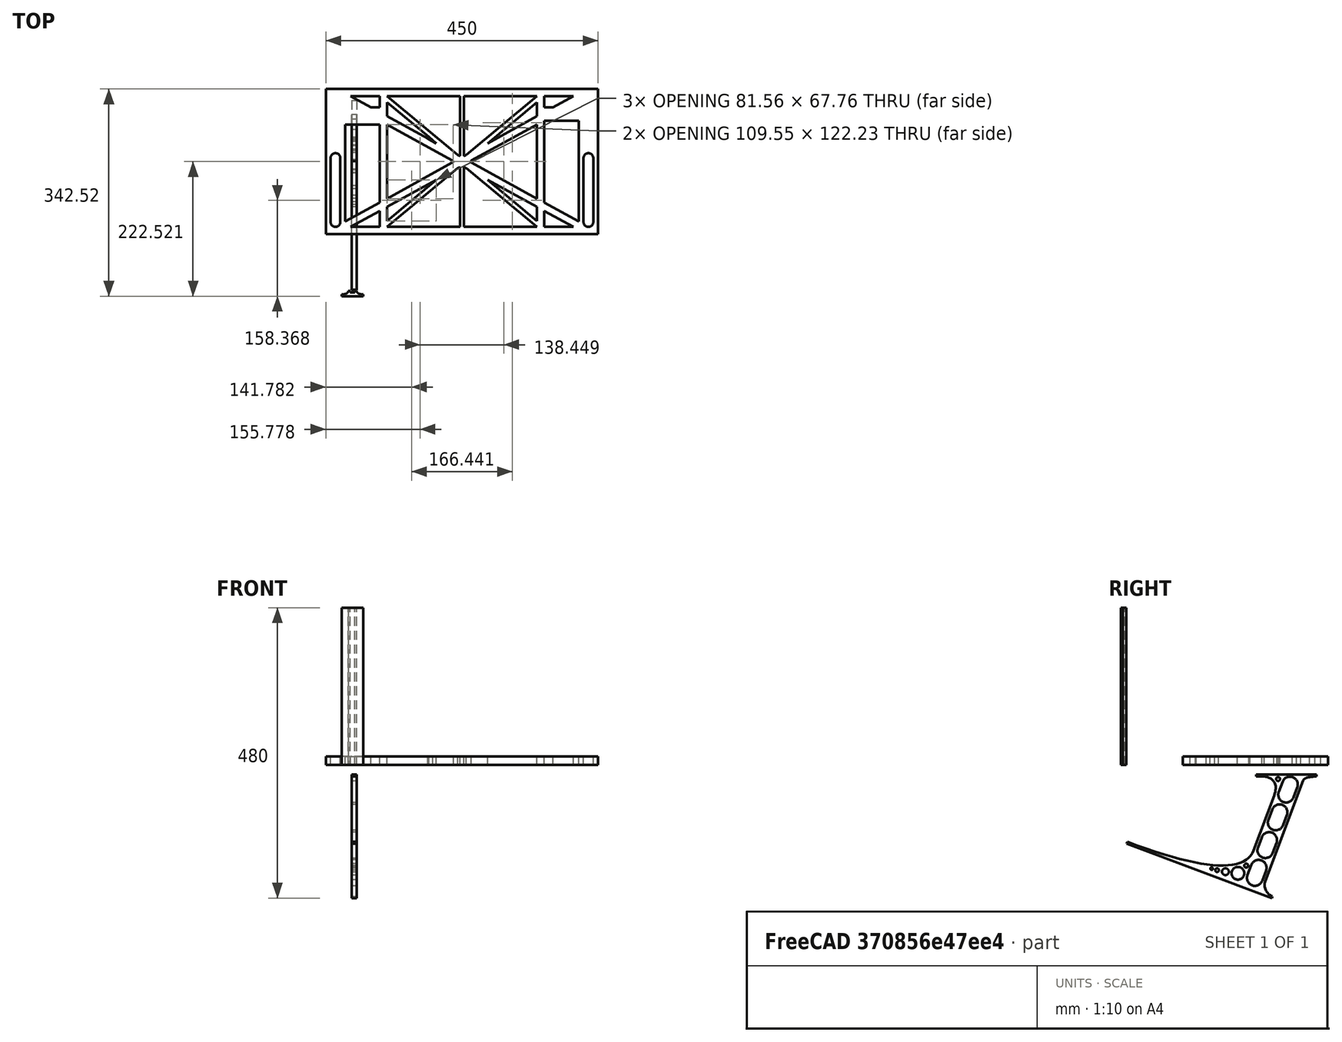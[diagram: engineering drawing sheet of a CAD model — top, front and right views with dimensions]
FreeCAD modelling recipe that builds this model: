
FCSTD DOCUMENT  (FreeCAD 0.19R0.19.2)
Label: laptopStand065
License: All rights reserved
LicenseURL: http://en.wikipedia.org/wiki/All_rights_reserved
objects: Sketcher::SketchObject×3, Part::Extrusion×3
note: 6 computed .brp shape members not serialized (recipe doc carries the construction recipe); baked Part::Feature solids carry a one-line shape summary decoded from their .brp

FEATURE [Sketcher::SketchObject] Sketch
  FullyConstrained = true
  sketch-geometry (104):
    g0: LineSegment StartX=-10.9272 StartY=-82.7794 StartZ=0 EndX=46.0728 EndY=-51.4823 EndZ=0
    g1: LineSegment StartX=366.073 StartY=-91.7794 StartZ=0 EndX=318.073 EndY=-65.424 EndZ=0
    g2: LineSegment StartX=-10.9272 StartY=77.3346 StartZ=0 EndX=-10.9272 EndY=-82.7794 EndZ=0
    g3: LineSegment StartX=375.073 StartY=-82.7794 StartZ=0 EndX=375.073 EndY=83.9235 EndZ=0
    g4: LineSegment StartX=-1.92719 StartY=-91.7794 StartZ=0 EndX=46.0728 EndY=-91.7794 EndZ=0
    g5: LineSegment StartX=318.073 StartY=124.221 StartZ=0 EndX=366.073 EndY=124.221 EndZ=0
    g6: LineSegment StartX=306.073 StartY=-81.8102 StartZ=0 EndX=224.513 EndY=-14.0532 EndZ=0
    g7: LineSegment StartX=306.073 StartY=124.221 StartZ=0 EndX=189.124 EndY=27.0628 EndZ=0
    g8: LineSegment StartX=58.0728 StartY=-91.7794 StartZ=0 EndX=175.022 EndY=5.37834 EndZ=0
    g9: LineSegment StartX=58.0728 StartY=-81.8102 StartZ=0 EndX=58.0728 EndY=-58.8351 EndZ=0
    g10: LineSegment StartX=306.073 StartY=114.251 StartZ=0 EndX=306.073 EndY=91.2763 EndZ=0
    g11: LineSegment StartX=224.513 StartY=46.4944 StartZ=0 EndX=306.073 EndY=114.251 EndZ=0
    g12: LineSegment StartX=175.022 StartY=27.0628 StartZ=0 EndX=58.0728 EndY=124.221 EndZ=0
    g13: LineSegment StartX=139.632 StartY=-14.0532 StartZ=0 EndX=58.0728 EndY=-81.8102 EndZ=0
    g14: LineSegment StartX=224.513 StartY=46.4944 StartZ=0 EndX=306.073 EndY=91.2763 EndZ=0
    g15: LineSegment StartX=139.632 StartY=-14.0532 StartZ=0 EndX=58.0728 EndY=-58.8351 EndZ=0
    g16: LineSegment StartX=189.124 StartY=5.37834 StartZ=0 EndX=306.073 EndY=-91.7794 EndZ=0
    g17: LineSegment StartX=306.073 StartY=77.3346 StartZ=0 EndX=306.073 EndY=-44.8935 EndZ=0
    g18: LineSegment StartX=318.073 StartY=83.9235 StartZ=0 EndX=318.073 EndY=-51.4823 EndZ=0
    g19: LineSegment StartX=306.073 StartY=-58.8351 StartZ=0 EndX=224.513 EndY=-14.0532 EndZ=0
    g20: LineSegment StartX=306.073 StartY=-58.8351 StartZ=0 EndX=306.073 EndY=-81.8102 EndZ=0
    g21: LineSegment StartX=318.073 StartY=-51.4823 StartZ=0 EndX=375.073 EndY=-82.7794 EndZ=0
    g22: LineSegment StartX=318.073 StartY=-65.424 StartZ=0 EndX=318.073 EndY=-91.7794 EndZ=0
    g23: LineSegment StartX=318.073 StartY=-91.7794 StartZ=0 EndX=366.073 EndY=-91.7794 EndZ=0
    g24: LineSegment StartX=58.0728 StartY=-44.8935 StartZ=0 EndX=58.0728 EndY=77.3346 EndZ=0
    g25: LineSegment StartX=46.0728 StartY=-65.424 StartZ=0 EndX=-1.92719 EndY=-91.7794 EndZ=0
    g26: LineSegment StartX=46.0728 StartY=-65.424 StartZ=0 EndX=46.0728 EndY=-91.7794 EndZ=0
    g27: LineSegment StartX=58.0728 StartY=91.2763 StartZ=0 EndX=58.0728 EndY=114.251 EndZ=0
    g28: LineSegment StartX=46.0728 StartY=77.3346 StartZ=0 EndX=46.0728 EndY=-51.4823 EndZ=0
    g29: LineSegment StartX=-42.9272 StartY=136.221 StartZ=0 EndX=-42.9272 EndY=-103.779 EndZ=0
    g30: LineSegment StartX=407.073 StartY=136.221 StartZ=0 EndX=407.073 EndY=-103.779 EndZ=0
    g31: LineSegment StartX=179.022 StartY=27.0628 StartZ=0 EndX=179.022 EndY=124.221 EndZ=0
    g32: LineSegment StartX=185.124 StartY=27.0628 StartZ=0 EndX=185.124 EndY=124.221 EndZ=0
    g33: ArcOfCircle CenterX=-26.9272 CenterY=22.1087 CenterZ=0 NormalX=0 NormalY=0 NormalZ=1 AngleXU=0 Radius=8 StartAngle=1e-16 EndAngle=3.14159
    g34: ArcOfCircle CenterX=-26.9272 CenterY=-83.7794 CenterZ=0 NormalX=0 NormalY=0 NormalZ=1 AngleXU=0 Radius=8 StartAngle=3.14159 EndAngle=6.28319
    g35: LineSegment StartX=-34.9272 StartY=22.1087 StartZ=0 EndX=-34.9272 EndY=-83.7794 EndZ=0
    g36: LineSegment StartX=-18.9272 StartY=22.1087 StartZ=0 EndX=-18.9272 EndY=-83.7794 EndZ=0
    g37: LineSegment StartX=185.124 StartY=-91.7794 StartZ=0 EndX=306.073 EndY=-91.7794 EndZ=0
    g38: LineSegment StartX=179.022 StartY=-91.7794 StartZ=0 EndX=58.0728 EndY=-91.7794 EndZ=0
    g39: LineSegment StartX=306.073 StartY=124.221 StartZ=0 EndX=185.124 EndY=124.221 EndZ=0
    g40: LineSegment StartX=179.022 StartY=124.221 StartZ=0 EndX=58.0728 EndY=124.221 EndZ=0
    g41: ArcOfCircle CenterX=391.073 CenterY=22.1087 CenterZ=0 NormalX=0 NormalY=0 NormalZ=1 AngleXU=0 Radius=8 StartAngle=-4.4e-15 EndAngle=3.14159
    g42: LineSegment StartX=399.073 StartY=22.1087 StartZ=0 EndX=399.073 EndY=-83.7794 EndZ=0
    g43: LineSegment StartX=383.073 StartY=22.1087 StartZ=0 EndX=383.073 EndY=-83.7794 EndZ=0
    g44: ArcOfCircle CenterX=391.073 CenterY=-83.7794 CenterZ=0 NormalX=0 NormalY=0 NormalZ=1 AngleXU=0 Radius=8 StartAngle=3.14159 EndAngle=6.28319
    g45: Circle CenterX=175.022 CenterY=27.0628 CenterZ=0 NormalX=0 NormalY=0 NormalZ=1 AngleXU=0 Radius=1
    g46: Circle CenterX=179.022 CenterY=24.8665 CenterZ=0 NormalX=0 NormalY=0 NormalZ=1 AngleXU=0 Radius=1
    g47: Circle CenterX=179.022 CenterY=27.0628 CenterZ=0 NormalX=0 NormalY=0 NormalZ=1 AngleXU=0 Radius=1
    g48: BSplineCurve PolesCount=3 KnotsCount=2 Degree=2 IsPeriodic=0
    g49: GeomPoint X=175.022 Y=27.0628 Z=0
    g50: GeomPoint X=179.022 Y=27.0628 Z=0
    g51: Circle CenterX=189.124 CenterY=27.0628 CenterZ=0 NormalX=0 NormalY=0 NormalZ=1 AngleXU=0 Radius=1
    g52: Circle CenterX=185.124 CenterY=24.8665 CenterZ=0 NormalX=0 NormalY=0 NormalZ=1 AngleXU=0 Radius=1
    g53: Circle CenterX=185.124 CenterY=27.0628 CenterZ=0 NormalX=0 NormalY=0 NormalZ=1 AngleXU=0 Radius=1
    g54: BSplineCurve PolesCount=3 KnotsCount=2 Degree=2 IsPeriodic=0
    g55: GeomPoint X=189.124 Y=27.0628 Z=0
    g56: GeomPoint X=185.124 Y=27.0628 Z=0
    g57: Circle CenterX=175.022 CenterY=5.37834 CenterZ=0 NormalX=0 NormalY=0 NormalZ=1 AngleXU=0 Radius=1
    g58: Circle CenterX=179.022 CenterY=7.57463 CenterZ=0 NormalX=0 NormalY=0 NormalZ=1 AngleXU=0 Radius=1
    g59: Circle CenterX=179.022 CenterY=5.34704 CenterZ=0 NormalX=0 NormalY=0 NormalZ=1 AngleXU=0 Radius=1
    g60: BSplineCurve PolesCount=3 KnotsCount=2 Degree=2 IsPeriodic=0
    g61: GeomPoint X=175.022 Y=5.37834 Z=0
    g62: GeomPoint X=179.022 Y=5.34704 Z=0
    g63: Circle CenterX=189.124 CenterY=5.37834 CenterZ=0 NormalX=0 NormalY=0 NormalZ=1 AngleXU=0 Radius=1
    g64: Circle CenterX=185.124 CenterY=7.57463 CenterZ=0 NormalX=0 NormalY=0 NormalZ=1 AngleXU=0 Radius=1
    g65: Circle CenterX=185.124 CenterY=5.34704 CenterZ=0 NormalX=0 NormalY=0 NormalZ=1 AngleXU=0 Radius=1
    g66: BSplineCurve PolesCount=3 KnotsCount=2 Degree=2 IsPeriodic=0
    g67: GeomPoint X=189.124 Y=5.37834 Z=0
    g68: GeomPoint X=185.124 Y=5.34704 Z=0
    g69: LineSegment StartX=179.022 StartY=5.34704 StartZ=0 EndX=179.022 EndY=-91.7794 EndZ=0
    g70: LineSegment StartX=185.124 StartY=-91.7794 StartZ=0 EndX=185.124 EndY=5.34704 EndZ=0
    g71: Circle CenterX=165.871 CenterY=18.1458 CenterZ=0 NormalX=0 NormalY=0 NormalZ=1 AngleXU=0 Radius=1
    g72: Circle CenterX=169.377 CenterY=16.2206 CenterZ=0 NormalX=0 NormalY=0 NormalZ=1 AngleXU=0 Radius=1
    g73: Circle CenterX=165.871 CenterY=14.2954 CenterZ=0 NormalX=0 NormalY=0 NormalZ=1 AngleXU=0 Radius=1
    g74: BSplineCurve PolesCount=3 KnotsCount=2 Degree=2 IsPeriodic=0
    g75: GeomPoint X=165.871 Y=18.1458 Z=0
    g76: GeomPoint X=165.871 Y=14.2954 Z=0
    g77: Circle CenterX=198.275 CenterY=18.1458 CenterZ=0 NormalX=0 NormalY=0 NormalZ=1 AngleXU=0 Radius=1
    g78: Circle CenterX=194.768 CenterY=16.2206 CenterZ=0 NormalX=0 NormalY=0 NormalZ=1 AngleXU=0 Radius=1
    g79: Circle CenterX=198.275 CenterY=14.2954 CenterZ=0 NormalX=0 NormalY=0 NormalZ=1 AngleXU=0 Radius=1
    g80: BSplineCurve PolesCount=3 KnotsCount=2 Degree=2 IsPeriodic=0
    g81: GeomPoint X=198.275 Y=18.1458 Z=0
    g82: GeomPoint X=198.275 Y=14.2954 Z=0
    g83: LineSegment StartX=165.871 StartY=18.1458 StartZ=0 EndX=58.0728 EndY=77.3346 EndZ=0
    g84: LineSegment StartX=58.0728 StartY=-44.8935 StartZ=0 EndX=165.871 EndY=14.2954 EndZ=0
    g85: LineSegment StartX=198.275 StartY=18.1458 StartZ=0 EndX=306.073 EndY=77.3346 EndZ=0
    g86: LineSegment StartX=198.275 StartY=14.2954 StartZ=0 EndX=306.073 EndY=-44.8935 EndZ=0
    g87: LineSegment StartX=407.073 StartY=-103.779 StartZ=0 EndX=-42.9272 EndY=-103.779 EndZ=0
    g88: LineSegment StartX=407.073 StartY=136.221 StartZ=0 EndX=-42.9272 EndY=136.221 EndZ=0
    g89: LineSegment StartX=46.0728 StartY=77.3346 StartZ=0 EndX=-10.9272 EndY=77.3346 EndZ=0
    g90: LineSegment StartX=46.0728 StartY=105.865 StartZ=0 EndX=31.5028 EndY=105.865 EndZ=0
    g91: LineSegment StartX=46.0728 StartY=124.221 StartZ=0 EndX=46.0728 EndY=105.865 EndZ=0
    g92: LineSegment StartX=-1.92719 StartY=124.221 StartZ=0 EndX=31.5028 EndY=105.865 EndZ=0
    g93: LineSegment StartX=46.0728 StartY=124.221 StartZ=0 EndX=-1.92719 EndY=124.221 EndZ=0
    g94: LineSegment StartX=318.073 StartY=83.9235 StartZ=0 EndX=375.073 EndY=83.9235 EndZ=0
    g95: LineSegment StartX=318.073 StartY=105.865 StartZ=0 EndX=332.643 EndY=105.865 EndZ=0
    g96: LineSegment StartX=332.643 StartY=105.865 StartZ=0 EndX=366.073 EndY=124.221 EndZ=0
    g97: LineSegment StartX=318.073 StartY=124.221 StartZ=0 EndX=318.073 EndY=105.865 EndZ=0
    g98: Circle CenterX=125.607 CenterY=54.1951 CenterZ=0 NormalX=0 NormalY=0 NormalZ=1 AngleXU=0 Radius=1
    g99: Circle CenterX=139.632 CenterY=46.4944 CenterZ=0 NormalX=0 NormalY=0 NormalZ=1 AngleXU=0 Radius=1
    g100: Circle CenterX=127.325 CenterY=56.7187 CenterZ=0 NormalX=0 NormalY=0 NormalZ=1 AngleXU=0 Radius=1
    g101: BSplineCurve PolesCount=3 KnotsCount=2 Degree=2 IsPeriodic=0
    g102: GeomPoint X=125.607 Y=54.1951 Z=0
    g103: GeomPoint X=127.325 Y=56.7187 Z=0
  constraints (194):
    c: Horizontal(g4)
    c: Horizontal(g5)
    c: Coincident(g11,g14)
    c: Coincident(g15,g13)
    c: Coincident(g19,g6)
    c: Coincident(g11,g10)
    c: Tangent(g10,g17)
    c: Coincident(g14,g10)
    c: Coincident(g20,g6)
    c: Tangent(g1,g19)
    c: Tangent(g17,g20)
    c: Coincident(g18,g21)
    c: Coincident(g22,g1)
    c: Tangent(g18,g22)
    c: Coincident(g13,g9)
    c: Tangent(g9,g24)
    c: Coincident(g15,g9)
    c: Tangent(g15,g25)
    c: Coincident(g26,g25)
    c: Coincident(g0,g28)
    c: Tangent(g24,g27)
    c: Block(g12)
    c: Block(g7)
    c: Block(g21)
    c: Block(g3)
    c: Block(g19)
    c: Block(g20)
    c: Block(g1)
    c: Block(g22)
    c: Block(g11)
    c: Block(g16)
    c: Block(g8)
    c: Block(g15)
    c: Block(g13)
    c: Block(g26)
    c: Block(g25)
    c: Block(g0)
    c: Block(g2)
    c: Block(g27)
    c: Block(g17)
    c: Block(g5)
    c: Block(g23)
    c: Block(g4)
    c: Vertical(g29)
    c: Vertical(g30)
    c: Block(g30)
    c: Block(g29)
    c: Vertical(g31)
    c: Vertical(g32)
    c: Block(g31)
    c: Block(g32)
    c: Tangent(g33,g36) = 1.5708
    c: Tangent(g33,g35) = -1.5708
    c: Tangent(g35,g34) = -1.5708
    c: Tangent(g36,g34) = 1.5708
    c: Vertical(g35)
    c: Equal(g33,g34)
    c: Block(g36)
    c: Block(g35)
    c: Coincident(g37,g16)
    c: Horizontal(g37)
    c: Coincident(g38,g8)
    c: Horizontal(g38)
    c: Coincident(g39,g7)
    c: Coincident(g39,g32)
    c: Horizontal(g39)
    c: Coincident(g40,g31)
    c: Coincident(g40,g12)
    c: Horizontal(g40)
    c: Tangent(g41,g42) = 1.5708
    c: Tangent(g42,g44) = 1.5708
    c: Equal(g41,g44)
    c: Coincident(g43,g41)
    c: Coincident(g43,g44)
    c: Block(g42)
    c: Block(g43)
    c: Coincident(g48,g12)
    c: Weight(g45) = 1
    c: Equal(g45,g46)
    c: Equal(g45,g47)
    c: Coincident(g48,g31)
    c: InternalAlignment(g45,g48)
    c: InternalAlignment(g46,g48)
    c: InternalAlignment(g47,g48)
    c: InternalAlignment(g49,g48)
    c: InternalAlignment(g50,g48)
    c: Coincident(g54,g7)
    c: Weight(g51) = 1
    c: Equal(g51,g52)
    c: Equal(g51,g53)
    c: Coincident(g54,g32)
    c: InternalAlignment(g51,g54)
    c: InternalAlignment(g52,g54)
    c: InternalAlignment(g53,g54)
    c: InternalAlignment(g55,g54)
    c: InternalAlignment(g56,g54)
    c: Block(g54)
    c: Block(g48)
    c: Coincident(g60,g8)
    c: Weight(g57) = 1
    c: Equal(g57,g58)
    c: Equal(g57,g59)
    c: InternalAlignment(g57,g60)
    c: InternalAlignment(g58,g60)
    c: InternalAlignment(g59,g60)
    c: InternalAlignment(g61,g60)
    c: InternalAlignment(g62,g60)
    c: Weight(g63) = 1
    c: Equal(g63,g64)
    c: Equal(g63,g65)
    c: InternalAlignment(g63,g66)
    c: InternalAlignment(g64,g66)
    c: InternalAlignment(g65,g66)
    c: InternalAlignment(g67,g66)
    c: InternalAlignment(g68,g66)
    c: Block(g66)
    c: Block(g60)
    c: Coincident(g69,g60)
    c: Coincident(g69,g38)
    c: Vertical(g69)
    c: Coincident(g70,g37)
    c: Coincident(g70,g66)
    c: Vertical(g70)
    c: Weight(g71) = 1
    c: Equal(g71,g72)
    c: Equal(g71,g73)
    c: InternalAlignment(g71,g74)
    c: InternalAlignment(g72,g74)
    c: InternalAlignment(g73,g74)
    c: InternalAlignment(g75,g74)
    c: InternalAlignment(g76,g74)
    c: Weight(g77) = 1
    c: Equal(g77,g78)
    c: Equal(g77,g79)
    c: InternalAlignment(g77,g80)
    c: InternalAlignment(g78,g80)
    c: InternalAlignment(g79,g80)
    c: InternalAlignment(g81,g80)
    c: InternalAlignment(g82,g80)
    c: Block(g74)
    c: Block(g80)
    c: Coincident(g83,g74)
    c: Coincident(g83,g24)
    c: Coincident(g84,g24)
    c: Coincident(g84,g74)
    c: Coincident(g85,g80)
    c: Coincident(g85,g17)
    c: Coincident(g86,g80)
    c: Coincident(g86,g17)
    c: Block(g24)
    c: Coincident(g87,g30)
    c: Coincident(g87,g29)
    c: Horizontal(g87)
    c: Distance(g87) = 450
    c: Coincident(g88,g30)
    c: Coincident(g88,g29)
    c: Horizontal(g88)
    c: Horizontal(g89)
    c: Coincident(g28,g89)
    c: Horizontal(g90)
    c: Vertical(g91)
    c: Block(g91)
    c: Block(g90)
    c: Block(g89)
    c: Distance(g91) = 18.3554
    c: Coincident(g93,g91)
    c: Coincident(g93,g92)
    c: Horizontal(g93)
    c: Block(g93)
    c: Block(g92)
    c: Coincident(g90,g92)
    c: Coincident(g2,g89)
    c: Coincident(g94,g18)
    c: Horizontal(g94)
    c: Horizontal(g95)
    c: Block(g94)
    c: Block(g10)
    c: Coincident(g96,g5)
    c: Coincident(g97,g5)
    c: Coincident(g97,g95)
    c: Vertical(g97)
    c: Block(g97)
    c: Coincident(g95,g96)
    c: Block(g96)
    c: Coincident(g3,g94)
    c: Weight(g98) = 1
    c: Equal(g98,g99)
    c: Equal(g98,g100)
    c: InternalAlignment(g98,g101)
    c: InternalAlignment(g99,g101)
    c: InternalAlignment(g100,g101)
    c: InternalAlignment(g102,g101)
    c: InternalAlignment(g103,g101)
    c: Block(g101)
FEATURE [Sketcher::SketchObject] Sketch001
  FullyConstrained = true
  MapMode = 4
  Placement = pos=(0,0,0) rot=(0.57735,0.57735,0.57735;2.0944rad)
  Support = -> [Sketch]
  sketch-geometry (46):
    g0: BSplineCurve PolesCount=3 KnotsCount=2 Degree=2 IsPeriodic=0
    g1: ArcOfCircle CenterX=73.1223 CenterY=-32.291 CenterZ=0 NormalX=0 NormalY=0 NormalZ=1 AngleXU=0 Radius=13 StartAngle=5.92268 EndAngle=9.06428
    g2: ArcOfCircle CenterX=66.7816 CenterY=-49.1439 CenterZ=0 NormalX=0 NormalY=0 NormalZ=1 AngleXU=0 Radius=13 StartAngle=2.78068 EndAngle=5.92131
    g3: ArcOfCircle CenterX=55.9263 CenterY=-78.1807 CenterZ=0 NormalX=0 NormalY=0 NormalZ=1 AngleXU=0 Radius=13 StartAngle=5.92268 EndAngle=9.06428
    g4: ArcOfCircle CenterX=49.5884 CenterY=-95.0342 CenterZ=0 NormalX=0 NormalY=0 NormalZ=1 AngleXU=0 Radius=13 StartAngle=2.78068 EndAngle=5.92131
    g5: ArcOfCircle CenterX=38.7206 CenterY=-124.067 CenterZ=0 NormalX=0 NormalY=0 NormalZ=1 AngleXU=0 Radius=13 StartAngle=5.92268 EndAngle=9.06428
    g6: ArcOfCircle CenterX=32.3875 CenterY=-140.92 CenterZ=0 NormalX=0 NormalY=0 NormalZ=1 AngleXU=0 Radius=13 StartAngle=2.78068 EndAngle=5.92131
    g7: ArcOfCircle CenterX=21.4715 CenterY=-169.934 CenterZ=0 NormalX=0 NormalY=0 NormalZ=1 AngleXU=0 Radius=13 StartAngle=5.92268 EndAngle=9.06428
    g8: ArcOfCircle CenterX=15.1336 CenterY=-186.787 CenterZ=0 NormalX=0 NormalY=0 NormalZ=1 AngleXU=0 Radius=13 StartAngle=2.78068 EndAngle=5.92131
    g9-g12: Circle x4 (B-spline internal-alignment scaffolding for g13; pole/knot coordinates omitted)
    g13: BSplineCurve PolesCount=4 KnotsCount=2 Degree=3 IsPeriodic=0
    g14: GeomPoint X=28.8094 Y=-19.0875 Z=0
    g15: GeomPoint X=47.0443 Y=-50.4712 Z=0
    g16: Circle CenterX=53.5586 CenterY=-23.2695 CenterZ=0 NormalX=0 NormalY=0 NormalZ=1 AngleXU=0 Radius=3.24518
    g17: Circle CenterX=-195.441 CenterY=-127.082 CenterZ=0 NormalX=0 NormalY=0 NormalZ=1 AngleXU=0 Radius=1
    g18: Circle CenterX=-8.24091 CenterY=-197.481 CenterZ=0 NormalX=0 NormalY=0 NormalZ=1 AngleXU=0 Radius=1
    g19: Circle CenterX=12.8789 CenterY=-141.321 CenterZ=0 NormalX=0 NormalY=0 NormalZ=1 AngleXU=0 Radius=1
    g20: BSplineCurve PolesCount=3 KnotsCount=2 Degree=2 IsPeriodic=0
    g21: GeomPoint X=-195.441 Y=-127.082 Z=0
    g22: GeomPoint X=12.8789 Y=-141.321 Z=0
    g23: Circle CenterX=-12.8016 CenterY=-179.036 CenterZ=0 NormalX=0 NormalY=0 NormalZ=1 AngleXU=0 Radius=10.5072
    g24: Circle CenterX=0.933922 CenterY=-166.43 CenterZ=0 NormalX=0 NormalY=0 NormalZ=1 AngleXU=0 Radius=3.26661
    g25: Circle CenterX=-33.5518 CenterY=-176.44 CenterZ=0 NormalX=0 NormalY=0 NormalZ=1 AngleXU=0 Radius=5.64388
    g26: Circle CenterX=-47.2366 CenterY=-173.859 CenterZ=0 NormalX=0 NormalY=0 NormalZ=1 AngleXU=0 Radius=3.01653
    g27: Circle CenterX=-56.2595 CenterY=-171.456 CenterZ=0 NormalX=0 NormalY=0 NormalZ=1 AngleXU=0 Radius=2.12826
    g28: ArcOfCircle CenterX=51.2151 CenterY=-198.473 CenterZ=0 NormalX=0 NormalY=0 NormalZ=1 AngleXU=0 Radius=20 StartAngle=2.78189 EndAngle=4.35269
    g29: LineSegment StartX=32.4951 StartY=-191.433 StartZ=0 EndX=94.6578 EndY=-26.1352 EndZ=0
    g30: LineSegment StartX=43.1192 StartY=-220.001 StartZ=0 EndX=-196.497 EndY=-129.89 EndZ=0
    g31: LineSegment StartX=43.1192 StartY=-220.001 StartZ=0 EndX=44.1752 EndY=-217.193 EndZ=0
    g32: LineSegment StartX=117.223 StartY=-19.0875 StartZ=0 EndX=117.223 EndY=-16.0875 EndZ=0
    g33: LineSegment StartX=117.223 StartY=-16.0875 StartZ=0 EndX=17.2232 EndY=-16.0875 EndZ=0
    g34: LineSegment StartX=17.2232 StartY=-16.0875 StartZ=0 EndX=17.2232 EndY=-19.0875 EndZ=0
    g35: LineSegment StartX=28.8094 StartY=-19.0875 StartZ=0 EndX=17.2232 EndY=-19.0875 EndZ=0
    g36: LineSegment StartX=47.0443 StartY=-50.4712 StartZ=0 EndX=12.8789 EndY=-141.321 EndZ=0
    g37: LineSegment StartX=-195.441 StartY=-127.082 StartZ=0 EndX=-196.497 EndY=-129.89 EndZ=0
    g38: LineSegment StartX=85.2866 StartY=-36.8766 StartZ=0 EndX=78.9396 EndY=-53.7463 EndZ=0
    g39: LineSegment StartX=60.9579 StartY=-27.7053 StartZ=0 EndX=54.6191 EndY=-44.5532 EndZ=0
    g40: LineSegment StartX=68.0907 StartY=-82.7664 StartZ=0 EndX=61.7465 EndY=-99.6365 EndZ=0
    g41: LineSegment StartX=43.7619 StartY=-73.595 StartZ=0 EndX=37.426 EndY=-90.4435 EndZ=0
    g42: LineSegment StartX=50.885 StartY=-128.652 StartZ=0 EndX=44.5456 EndY=-145.522 EndZ=0
    g43: LineSegment StartX=26.5562 StartY=-119.481 StartZ=0 EndX=20.2251 EndY=-136.329 EndZ=0
    g44: LineSegment StartX=9.3071 StartY=-165.349 StartZ=0 EndX=2.97115 EndY=-182.197 EndZ=0
    g45: LineSegment StartX=33.6358 StartY=-174.52 StartZ=0 EndX=27.2917 EndY=-191.39 EndZ=0
  constraints (71):
    c: Block(g0)
    c: Block(g1)
    c: Block(g2)
    c: Block(g4)
    c: Block(g3)
    c: Block(g6)
    c: Block(g5)
    c: Block(g8)
    c: Block(g7)
    c: Weight(g9) = 1
    c: Equal(g9,g10)
    c: Equal(g9,g11)
    c: Equal(g9,g12)
    c: InternalAlignment(g9-g12 -> g13) x4
    c: InternalAlignment(g14,g13)
    c: InternalAlignment(g15,g13)
    c: Block(g16)
    c: Weight(g17) = 1
    c: Equal(g17,g18)
    c: Equal(g17,g19)
    c: InternalAlignment(g17,g20)
    c: InternalAlignment(g18,g20)
    c: InternalAlignment(g19,g20)
    c: InternalAlignment(g21,g20)
    c: InternalAlignment(g22,g20)
    c: Block(g20)
    c: Block(g23)
    c: Block(g24)
    c: Block(g25)
    c: Block(g26)
    c: Block(g27)
    c: Block(g28)
    c: Coincident(g29,g28)
    c: Coincident(g29,g0)
    c: Block(g13)
    c: Coincident(g31,g30)
    c: Coincident(g31,g28)
    c: Block(g31)
    c: Coincident(g32,g0)
    c: Vertical(g32)
    c: Coincident(g33,g32)
    c: Horizontal(g33)
    c: Coincident(g34,g33)
    c: Vertical(g34)
    c: Block(g33)
    c: Coincident(g35,g13)
    c: Coincident(g35,g34)
    c: Horizontal(g35)
    c: Coincident(g36,g13)
    c: Coincident(g36,g20)
    c: Coincident(g37,g20)
    c: Coincident(g37,g30)
    c: Block(g30)
    c: Coincident(g38,g1)
    c: Coincident(g38,g2)
    c: Coincident(g39,g1)
    c: Coincident(g39,g2)
    c: Coincident(g40,g3)
    c: Coincident(g40,g4)
    c: Coincident(g41,g3)
    c: Coincident(g41,g4)
    c: Coincident(g42,g5)
    c: Coincident(g42,g6)
    c: Coincident(g43,g5)
    c: Coincident(g43,g6)
    c: Coincident(g44,g7)
    c: Coincident(g44,g8)
    c: Coincident(g45,g7)
    c: Coincident(g45,g8)
    c: Distance(g30) = 256
    c: Distance(g33) = 100
FEATURE [Part::Extrusion] Extrude002
  Base = -> Sketch001
  Dir = (1,0,0)
  DirMode = 2
  FaceMakerClass = Part::FaceMakerBullseye
  LengthFwd = 8
  LengthRev = 0
  Solid = true
  Symmetric = false
FEATURE [Sketcher::SketchObject] Sketch002
  FullyConstrained = true
  sketch-geometry (20):
    g0: LineSegment StartX=-2.77179 StartY=-200.304 StartZ=0 EndX=5.22821 EndY=-200.304 EndZ=0
    g1: LineSegment StartX=5.22821 StartY=-200.304 StartZ=0 EndX=5.22821 EndY=-197.304 EndZ=0
    g2: LineSegment StartX=-2.77179 StartY=-200.304 StartZ=0 EndX=-2.77179 EndY=-197.304 EndZ=0
    g3: LineSegment StartX=5.22821 StartY=-197.304 StartZ=0 EndX=8.22821 EndY=-197.304 EndZ=0
    g4: LineSegment StartX=-2.77179 StartY=-197.304 StartZ=0 EndX=-5.77179 EndY=-197.304 EndZ=0
    g5: LineSegment StartX=19.2282 StartY=-203.304 StartZ=0 EndX=19.2282 EndY=-206.304 EndZ=0
    g6: LineSegment StartX=-16.7718 StartY=-203.304 StartZ=0 EndX=-16.7718 EndY=-206.304 EndZ=0
    g7: LineSegment StartX=-16.7718 StartY=-206.304 StartZ=0 EndX=19.2282 EndY=-206.304 EndZ=0
    g8: Circle CenterX=-16.7718 CenterY=-203.304 CenterZ=0 NormalX=0 NormalY=0 NormalZ=1 AngleXU=0 Radius=1
    g9: Circle CenterX=-5.77179 CenterY=-203.304 CenterZ=0 NormalX=0 NormalY=0 NormalZ=1 AngleXU=0 Radius=1
    g10: Circle CenterX=-5.77179 CenterY=-197.304 CenterZ=0 NormalX=0 NormalY=0 NormalZ=1 AngleXU=0 Radius=1
    g11: BSplineCurve PolesCount=3 KnotsCount=2 Degree=2 IsPeriodic=0
    g12: GeomPoint X=-16.7718 Y=-203.304 Z=0
    g13: GeomPoint X=-5.77179 Y=-197.304 Z=0
    g14: Circle CenterX=19.2282 CenterY=-203.304 CenterZ=0 NormalX=0 NormalY=0 NormalZ=1 AngleXU=0 Radius=1
    g15: Circle CenterX=8.22821 CenterY=-203.304 CenterZ=0 NormalX=0 NormalY=0 NormalZ=1 AngleXU=0 Radius=1
    g16: Circle CenterX=8.22821 CenterY=-197.304 CenterZ=0 NormalX=0 NormalY=0 NormalZ=1 AngleXU=0 Radius=1
    g17: BSplineCurve PolesCount=3 KnotsCount=2 Degree=2 IsPeriodic=0
    g18: GeomPoint X=19.2282 Y=-203.304 Z=0
    g19: GeomPoint X=8.22821 Y=-197.304 Z=0
  constraints (41):
    c: Horizontal(g0)
    c: Distance(g0) = 8
    c: Coincident(g1,g0)
    c: Vertical(g1)
    c: Distance(g1) = 3
    c: Coincident(g2,g0)
    c: Vertical(g2)
    c: Distance(g2) = 3
    c: Coincident(g3,g1)
    c: Horizontal(g3)
    c: Distance(g3) = 3
    c: Coincident(g4,g2)
    c: Horizontal(g4)
    c: Distance(g4) = 3
    c: Vertical(g5)
    c: Vertical(g6)
    c: Coincident(g7,g6)
    c: Coincident(g7,g5)
    c: Weight(g8) = 1
    c: Equal(g8,g9)
    c: Equal(g8,g10)
    c: Coincident(g11,g4)
    c: InternalAlignment(g8,g11)
    c: InternalAlignment(g9,g11)
    c: InternalAlignment(g10,g11)
    c: InternalAlignment(g12,g11)
    c: InternalAlignment(g13,g11)
    c: Coincident(g17,g5)
    c: Weight(g14) = 1
    c: Equal(g14,g15)
    c: Equal(g14,g16)
    c: Coincident(g17,g3)
    c: InternalAlignment(g14,g17)
    c: InternalAlignment(g15,g17)
    c: InternalAlignment(g16,g17)
    c: InternalAlignment(g18,g17)
    c: InternalAlignment(g19,g17)
    c: Block(g7)
    c: Block(g17)
    c: Block(g11)
    c: Block(g6)
FEATURE [Part::Extrusion] Extrude003
  Base = -> Sketch002
  Dir = (0,0,1)
  DirMode = 2
  FaceMakerClass = Part::FaceMakerBullseye
  LengthFwd = 260
  LengthRev = 0
  Solid = true
  Symmetric = false
FEATURE [Part::Extrusion] Extrude
  Base = -> Sketch
  Dir = (0,0,1)
  DirMode = 2
  FaceMakerClass = Part::FaceMakerBullseye
  LengthFwd = 14
  LengthRev = 0
  Solid = true
  Symmetric = false
